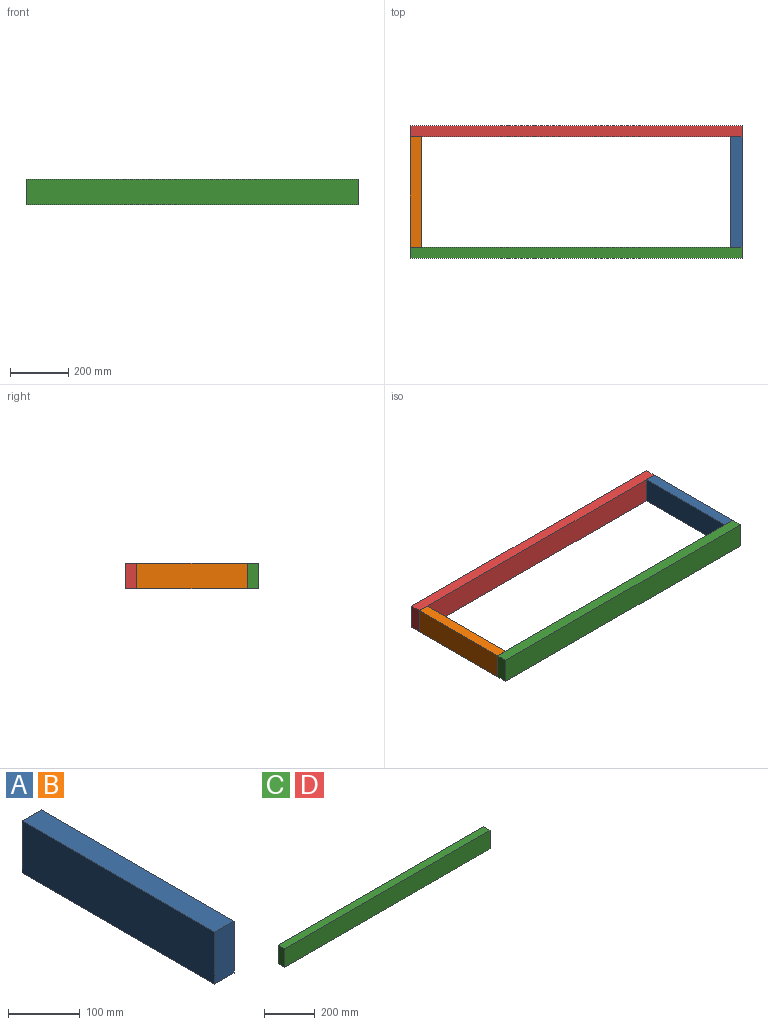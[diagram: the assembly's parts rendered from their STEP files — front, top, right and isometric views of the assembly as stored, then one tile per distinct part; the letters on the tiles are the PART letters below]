
ASSEMBLY  parts=4 mates=9
PART A: 6 faces, bbox 38.1x381x88.9 mm
  f0: plane 381x88.9mm, normal (1,0,0), area 33870.9mm2, adj f1,f3,f4,f5
  f1: plane 381x38.1mm, normal (0,0,1), area 14516.1mm2, adj f0,f2,f4,f5
  f2: plane 381x88.9mm, normal (-1,0,0), area 33870.9mm2, adj f1,f3,f4,f5
  f3: plane 381x38.1mm, normal (0,0,-1), area 14516.1mm2, adj f0,f2,f4,f5
  f4: plane 88.9x38.1mm, normal (0,-1,0), area 3387.1mm2, adj f0,f1,f2,f3
  f5: plane 88.9x38.1mm, normal (0,1,0), area 3387.1mm2, adj f0,f1,f2,f3
PART B: same geometry as A
PART C: 6 faces, bbox 1143x38.1x88.9 mm
  f0: plane 1143x88.9mm, normal (0,1,0), area 101612.7mm2, adj f1,f3,f4,f5
  f1: plane 1143x38.1mm, normal (0,0,1), area 43548.3mm2, adj f0,f2,f4,f5
  f2: plane 1143x88.9mm, normal (0,-1,0), area 101612.7mm2, adj f1,f3,f4,f5
  f3: plane 1143x38.1mm, normal (0,0,-1), area 43548.3mm2, adj f0,f2,f4,f5
  f4: plane 88.9x38.1mm, normal (1,0,0), area 3387.1mm2, adj f0,f1,f2,f3
  f5: plane 88.9x38.1mm, normal (-1,0,0), area 3387.1mm2, adj f0,f1,f2,f3
PART D: same geometry as C
PLACE A t=(385.73,-143.31,-15.68)mm
PLACE B t=(-719.17,-143.31,-15.68)mm
PLACE C t=(-738.22,-543.36,-15.68)mm
PLACE D t=(-738.22,-124.26,-15.68)mm fixed
MATE planar C.f1 <-> D.f1  axis (0,0,1) through (-166.72,-543.36,28.77)mm
MATE planar A.f5 <-> D.f2  axis (0,1,0) through (385.73,-143.31,-15.68)mm
MATE planar B.f5 <-> D.f2  axis (0,1,0) through (-719.17,-143.31,-15.68)mm
MATE planar A.f0 <-> D.f4  axis (1,0,0) through (404.78,-333.81,-15.68)mm
MATE planar A.f1 <-> D.f1  axis (0,0,1) through (385.73,-333.81,28.77)mm
MATE planar C.f0 <-> A.f4  axis (0,1,0) through (-166.72,-524.31,-15.68)mm
MATE planar B.f1 <-> D.f1  axis (0,0,1) through (-719.17,-333.81,28.77)mm
MATE planar B.f2 <-> D.f5  axis (-1,0,0) through (-738.22,-333.81,-15.68)mm
MATE planar C.f4 <-> A.f0  axis (1,0,0) through (404.78,-543.36,-15.68)mm
